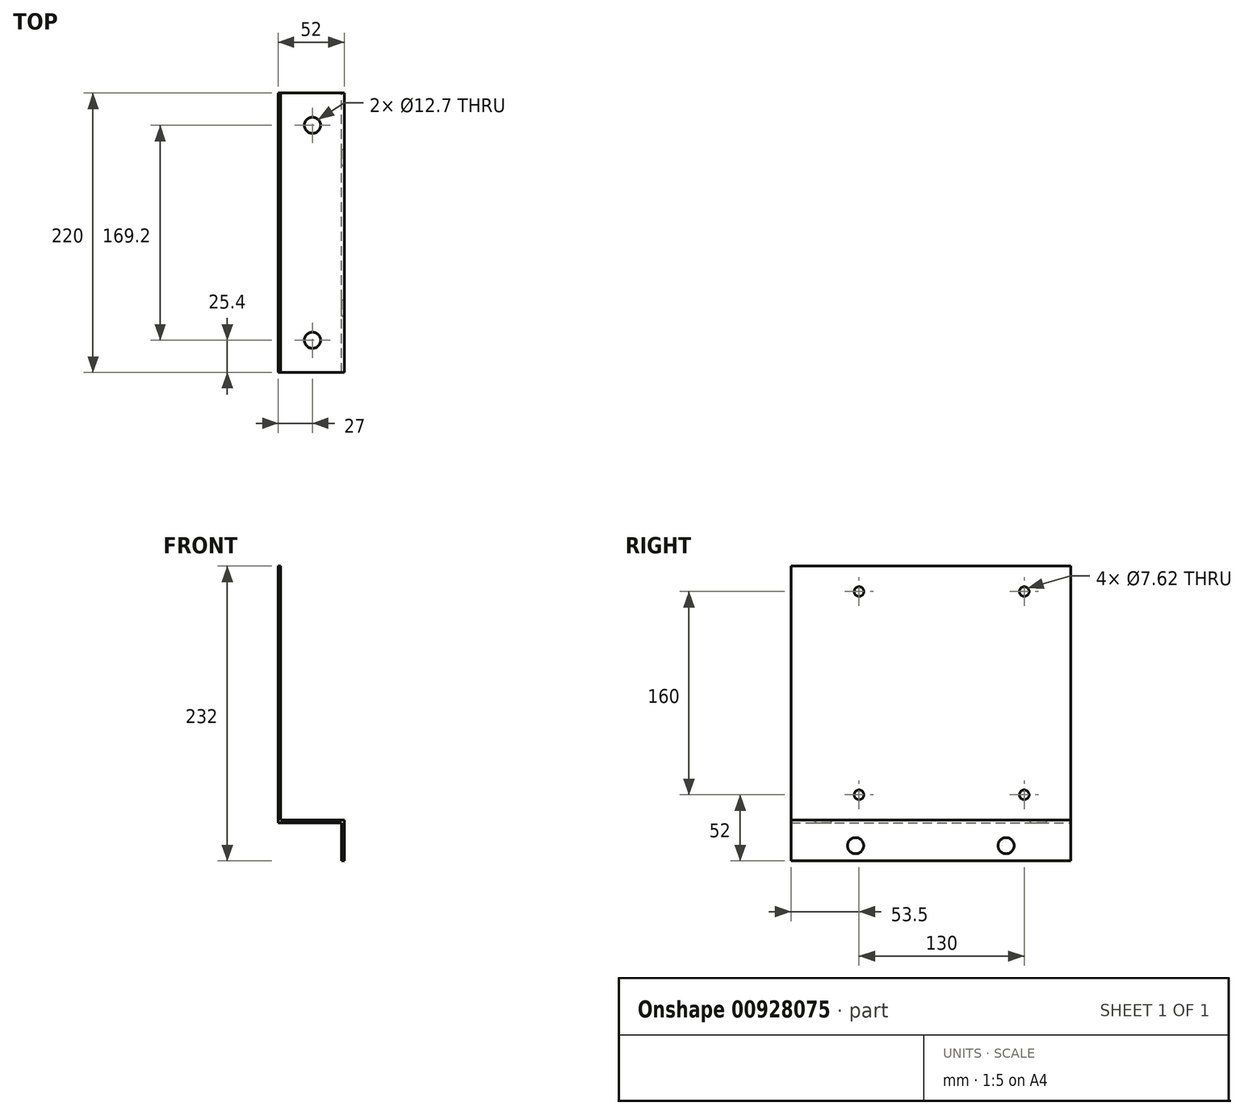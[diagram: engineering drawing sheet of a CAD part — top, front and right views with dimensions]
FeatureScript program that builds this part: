
annotation { "Feature Type Name" : "Feature", "Feature Type Description" : "" }
export const myFeature = defineFeature(function(context is Context, id is Id, definition is map)
    precondition{}
    {
        {
            var Q0;
            Q0=qCreatedBy(makeId("Front.planeOp"),FACE);
            var sketch = newSketch(context, id + "F0", { "sketchPlane" : qUnion([Q0])});
            skLineSegment(sketch, "E0", {"start": v(0, -30) * mm, "end": v(2, -30) * mm});
            skLineSegment(sketch, "E1", {"start": v(2, -30) * mm, "end": v(2, 2) * mm});
            skLineSegment(sketch, "E2", {"start": v(2, 2) * mm, "end": v(-48, 2) * mm});
            skLineSegment(sketch, "E3", {"start": v(-48, 2) * mm, "end": v(-48, 202) * mm});
            skLineSegment(sketch, "E4", {"start": v(-48, 202) * mm, "end": v(-50, 202) * mm});
            skLineSegment(sketch, "E5", {"start": v(-50, 202) * mm, "end": v(-50, 0) * mm});
            skLineSegment(sketch, "E6", {"start": v(-50, 0) * mm, "end": v(0, 0) * mm});
            skLineSegment(sketch, "E7", {"start": v(0, 0) * mm, "end": v(0, -30) * mm});
            skSolve(sketch);
        }
        {
            var Q0;
            Q0=makeQuery(id+"F0.imprint","IMPRINT",FACE,{"disambiguationData":[TD([[makeQuery(id+"F0.imprint","IMPRINT",EDGE,{"derivedFrom":sQuery(id+"F0.wireOp",EDGE,"E0")}),1.0]])]});
            extrude(context, id + "F1", {"entities" : qUnion([Q0]), "depth" : 220 * mm, "offsetDistance" : 25.4 * mm});
        }
        {
            var Q0;
            Q0=makeQuery(id+"F1.opExtrude","SWEPT_FACE",FACE,{"disambiguationData":[OSD([sQuery(id+"F0.wireOp",EDGE,"E1")])]});
            var sketch = newSketch(context, id + "F2", { "sketchPlane" : qUnion([Q0])});
            skCircle(sketch, "E8", {"center": v(-169.2, -18.05) * mm, "radius": 9.37 * mm});
            skPoint(sketch, "E8.centerSnap0", {"position": v(-220, -18.05) * mm});
            skCircle(sketch, "E9", {"center": v(-50.8, -18.05) * mm, "radius": 9.37 * mm});
            skSolve(sketch);
        }
        {
            var Q0;
            Q0=sQuery(id+"F2.wireOp",VERTEX,"E8.center");
            var Q1;
            Q1=sQuery(id+"F2.wireOp",VERTEX,"E9.center");
            var Q2;
            Q2=makeQuery(id+"F1.opExtrude","SWEPT_BODY",BODY,{"disambiguationData":[OSD([sQuery(id+"F0.wireOp",EDGE,"E0"),sQuery(id+"F0.wireOp",EDGE,"E1"),sQuery(id+"F0.wireOp",EDGE,"E2"),sQuery(id+"F0.wireOp",EDGE,"E3"),sQuery(id+"F0.wireOp",EDGE,"E4"),sQuery(id+"F0.wireOp",EDGE,"E5"),sQuery(id+"F0.wireOp",EDGE,"E6"),sQuery(id+"F0.wireOp",EDGE,"E7")])]});
            hole(context, id + "F3", {"style" : HoleStyle.SIMPLE, "endStyle" : HoleEndStyle.THROUGH, "holeDiameter" : 12.7 * mm, "majorDiameter" : 6.35 * mm, "isTappedThrough" : true, "tappedDepth" : 12.7 * mm, "tapClearance" : 3, "locations" : qUnion([Q0, Q1]), "scope" : qUnion([Q2])});
        }
        {
            var Q0;
            Q0=makeQuery(id+"F1.opExtrude","SWEPT_FACE",FACE,{"disambiguationData":[OSD([sQuery(id+"F0.wireOp",EDGE,"E3")])]});
            var sketch = newSketch(context, id + "F4", { "sketchPlane" : qUnion([Q0])});
            skCircle(sketch, "E10", {"center": v(-166.5, 22) * mm, "radius": 6.35 * mm});
            skCircle(sketch, "E11", {"center": v(-36.5, 22) * mm, "radius": 6.35 * mm});
            skCircle(sketch, "E12", {"center": v(-36.5, 182) * mm, "radius": 6.35 * mm});
            skCircle(sketch, "E13", {"center": v(-166.5, 182) * mm, "radius": 6.35 * mm});
            skLineSegment(sketch, "E14", {"start": v(-166.5, 182) * mm, "end": v(-36.5, 182) * mm});
            skLineSegment(sketch, "E15", {"start": v(-166.5, 182) * mm, "end": v(-220, 182) * mm});
            skLineSegment(sketch, "E16", {"start": v(-36.5, 182) * mm, "end": v(0, 182) * mm});
            skLineSegment(sketch, "E17", {"start": v(-166.5, 22) * mm, "end": v(-220, 22) * mm});
            skSolve(sketch);
        }
        {
            var Q0;
            Q0=sQuery(id+"F4.wireOp",VERTEX,"E13.center");
            var Q1;
            Q1=sQuery(id+"F4.wireOp",VERTEX,"E12.center");
            var Q2;
            Q2=sQuery(id+"F4.wireOp",VERTEX,"E11.center");
            var Q3;
            Q3=sQuery(id+"F4.wireOp",VERTEX,"E10.center");
            var Q4;
            Q4=makeQuery(id+"F1.opExtrude","SWEPT_BODY",BODY,{"disambiguationData":[OSD([sQuery(id+"F0.wireOp",EDGE,"E0"),sQuery(id+"F0.wireOp",EDGE,"E1"),sQuery(id+"F0.wireOp",EDGE,"E2"),sQuery(id+"F0.wireOp",EDGE,"E3"),sQuery(id+"F0.wireOp",EDGE,"E4"),sQuery(id+"F0.wireOp",EDGE,"E5"),sQuery(id+"F0.wireOp",EDGE,"E6"),sQuery(id+"F0.wireOp",EDGE,"E7")])]});
            hole(context, id + "F5", {"style" : HoleStyle.SIMPLE, "endStyle" : HoleEndStyle.THROUGH, "holeDiameter" : 7.62 * mm, "majorDiameter" : 6.35 * mm, "isTappedThrough" : true, "tappedDepth" : 12.7 * mm, "tapClearance" : 3, "locations" : qUnion([Q0, Q1, Q2, Q3]), "scope" : qUnion([Q4])});
        }
        {
            var Q0;
            Q0=makeQuery(id+"F1.opExtrude","SWEPT_FACE",FACE,{"disambiguationData":[OSD([sQuery(id+"F0.wireOp",EDGE,"E2")])]});
            var sketch = newSketch(context, id + "F6", { "sketchPlane" : qUnion([Q0])});
            skCircle(sketch, "E18", {"center": v(-23, -25.4) * mm, "radius": 9.23 * mm});
            skPoint(sketch, "E18.centerSnap0", {"position": v(-23, 0) * mm});
            skCircle(sketch, "E19", {"center": v(-23, -194.6) * mm, "radius": 9.23 * mm});
            skSolve(sketch);
        }
        {
            var Q0;
            Q0=sQuery(id+"F6.wireOp",VERTEX,"E18.center");
            var Q1;
            Q1=sQuery(id+"F6.wireOp",VERTEX,"E19.center");
            var Q2;
            Q2=makeQuery(id+"F1.opExtrude","SWEPT_BODY",BODY,{"disambiguationData":[OSD([sQuery(id+"F0.wireOp",EDGE,"E0"),sQuery(id+"F0.wireOp",EDGE,"E1"),sQuery(id+"F0.wireOp",EDGE,"E2"),sQuery(id+"F0.wireOp",EDGE,"E3"),sQuery(id+"F0.wireOp",EDGE,"E4"),sQuery(id+"F0.wireOp",EDGE,"E5"),sQuery(id+"F0.wireOp",EDGE,"E6"),sQuery(id+"F0.wireOp",EDGE,"E7")])]});
            hole(context, id + "F7", {"style" : HoleStyle.SIMPLE, "endStyle" : HoleEndStyle.THROUGH, "holeDiameter" : 12.7 * mm, "majorDiameter" : 6.35 * mm, "isTappedThrough" : true, "tappedDepth" : 12.7 * mm, "tapClearance" : 3, "locations" : qUnion([Q0, Q1]), "scope" : qUnion([Q2])});
        }
    });
